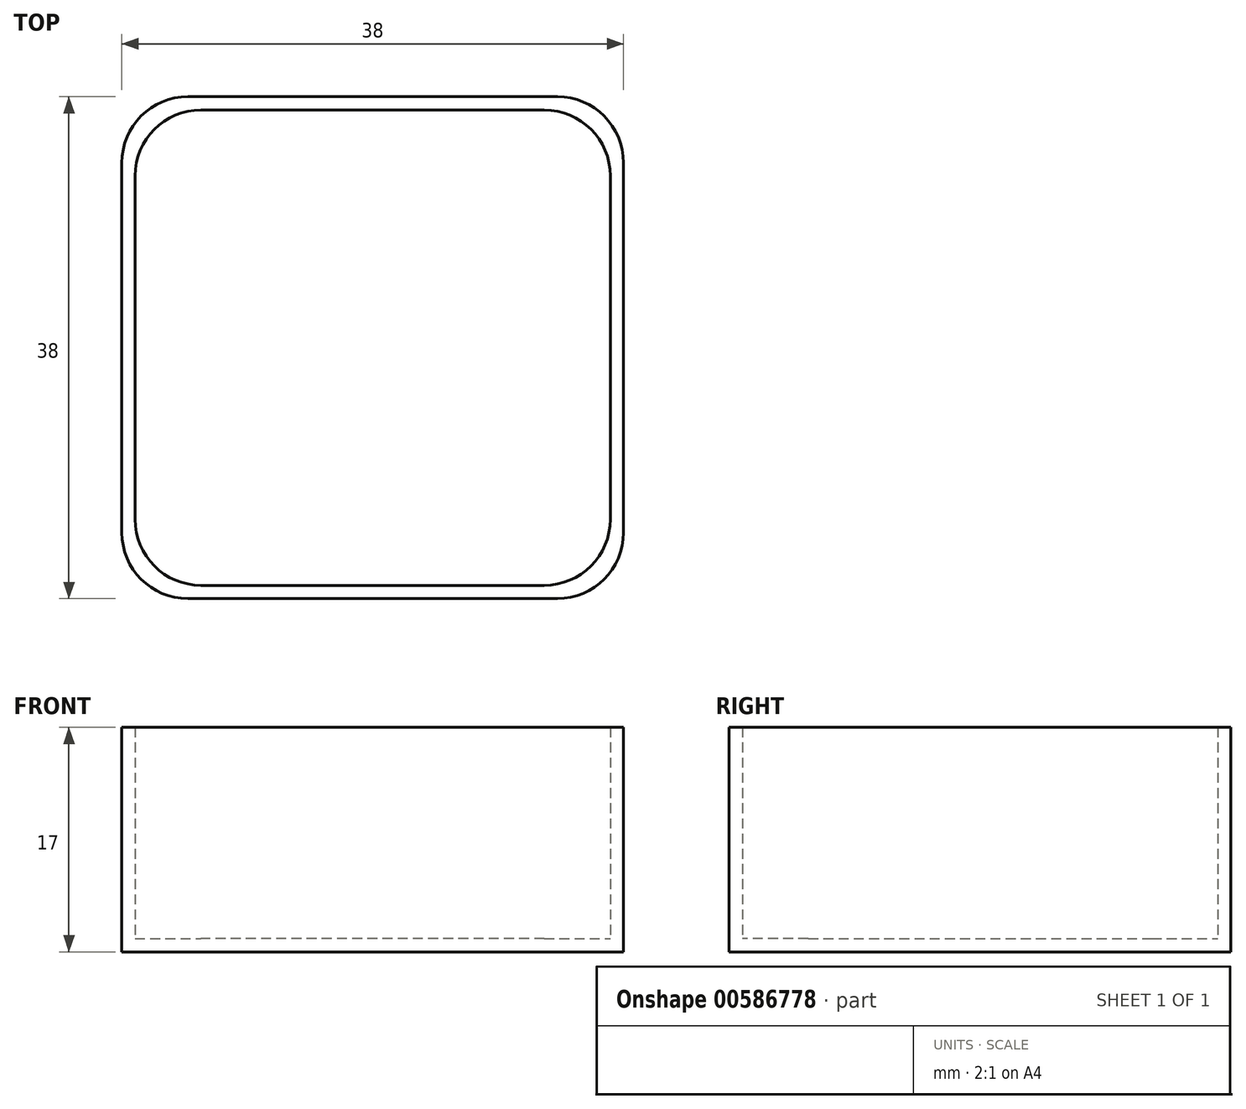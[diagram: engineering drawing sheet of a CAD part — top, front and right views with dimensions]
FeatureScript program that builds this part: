
annotation { "Feature Type Name" : "Feature", "Feature Type Description" : "" }
export const myFeature = defineFeature(function(context is Context, id is Id, definition is map)
    precondition{}
    {
        {
            var Q0;
            Q0=qCreatedBy(makeId("Top.planeOp"),FACE);
            var sketch = newSketch(context, id + "F0", { "sketchPlane" : qUnion([Q0])});
            skLineSegment(sketch, "E0.bottom", {"start": v(19, -19) * mm, "end": v(-19, -19) * mm});
            skLineSegment(sketch, "E0.top", {"start": v(19, 19) * mm, "end": v(-19, 19) * mm});
            skLineSegment(sketch, "E0.left", {"start": v(19, -19) * mm, "end": v(19, 19) * mm});
            skLineSegment(sketch, "E0.right", {"start": v(-19, -19) * mm, "end": v(-19, 19) * mm});
            skPoint(sketch, "E0.middle", {"position": v(0, 0) * mm});
            skLineSegment(sketch, "E1.bottom", {"start": v(18, -18) * mm, "end": v(-18, -18) * mm});
            skLineSegment(sketch, "E1.top", {"start": v(18, 18) * mm, "end": v(-18, 18) * mm});
            skLineSegment(sketch, "E1.left", {"start": v(18, -18) * mm, "end": v(18, 18) * mm});
            skLineSegment(sketch, "E1.right", {"start": v(-18, -18) * mm, "end": v(-18, 18) * mm});
            skSolve(sketch);
        }
        {
            var Q0;
            Q0=makeQuery(id+"F0.imprint","IMPRINT",FACE,{"disambiguationData":[TD([[makeQuery(id+"F0.imprint","IMPRINT",EDGE,{"derivedFrom":sQuery(id+"F0.wireOp",EDGE,"E1.bottom")}),-1.0]])]});
            extrude(context, id + "F1", {"entities" : qUnion([Q0]), "depth" : 1 * mm, "offsetDistance" : 25 * mm});
        }
        {
            var Q0;
            Q0=makeQuery(id+"F0.imprint","IMPRINT",FACE,{"disambiguationData":[TD([[makeQuery(id+"F0.imprint","IMPRINT",EDGE,{"derivedFrom":sQuery(id+"F0.wireOp",EDGE,"E0.bottom")}),-1.0]])]});
            extrude(context, id + "F2", {"entities" : qUnion([Q0]), "operationType" : NewBodyOperationType.ADD, "depth" : 17 * mm, "offsetDistance" : 25 * mm});
        }
        {
            var Q0;
            Q0=makeQuery(id+"F2.opExtrude","SWEPT_EDGE",EDGE,{"disambiguationData":[OSD([sQuery(id+"F0.wireOp",EDGE,"E1.top"),sQuery(id+"F0.wireOp",EDGE,"E1.right")])]});
            var Q1;
            Q1=makeQuery(id+"F2.opExtrude","SWEPT_EDGE",EDGE,{"disambiguationData":[OSD([sQuery(id+"F0.wireOp",EDGE,"E1.top"),sQuery(id+"F0.wireOp",EDGE,"E1.left")])]});
            var Q2;
            Q2=makeQuery(id+"F2.opExtrude","SWEPT_EDGE",EDGE,{"disambiguationData":[OSD([sQuery(id+"F0.wireOp",EDGE,"E1.bottom"),sQuery(id+"F0.wireOp",EDGE,"E1.left")])]});
            var Q3;
            Q3=makeQuery(id+"F2.opExtrude","SWEPT_EDGE",EDGE,{"disambiguationData":[OSD([sQuery(id+"F0.wireOp",EDGE,"E1.bottom"),sQuery(id+"F0.wireOp",EDGE,"E1.right")])]});
            var Q4;
            Q4=makeQuery(id+"F2.opExtrude","SWEPT_EDGE",EDGE,{"disambiguationData":[OSD([sQuery(id+"F0.wireOp",EDGE,"E0.top"),sQuery(id+"F0.wireOp",EDGE,"E0.right")])]});
            var Q5;
            Q5=makeQuery(id+"F2.opExtrude","SWEPT_EDGE",EDGE,{"disambiguationData":[OSD([sQuery(id+"F0.wireOp",EDGE,"E0.bottom"),sQuery(id+"F0.wireOp",EDGE,"E0.right")])]});
            var Q6;
            Q6=makeQuery(id+"F2.opExtrude","SWEPT_EDGE",EDGE,{"disambiguationData":[OSD([sQuery(id+"F0.wireOp",EDGE,"E0.bottom"),sQuery(id+"F0.wireOp",EDGE,"E0.left")])]});
            var Q7;
            Q7=makeQuery(id+"F2.opExtrude","SWEPT_EDGE",EDGE,{"disambiguationData":[OSD([sQuery(id+"F0.wireOp",EDGE,"E0.top"),sQuery(id+"F0.wireOp",EDGE,"E0.left")])]});
            fillet(context, id + "F3", {"entities" : qUnion([Q0, Q1, Q2, Q3, Q4, Q5, Q6, Q7]), "radius" : 5 * mm, "tangentPropagation" : true, "allowEdgeOverflow" : false});
        }
    });
